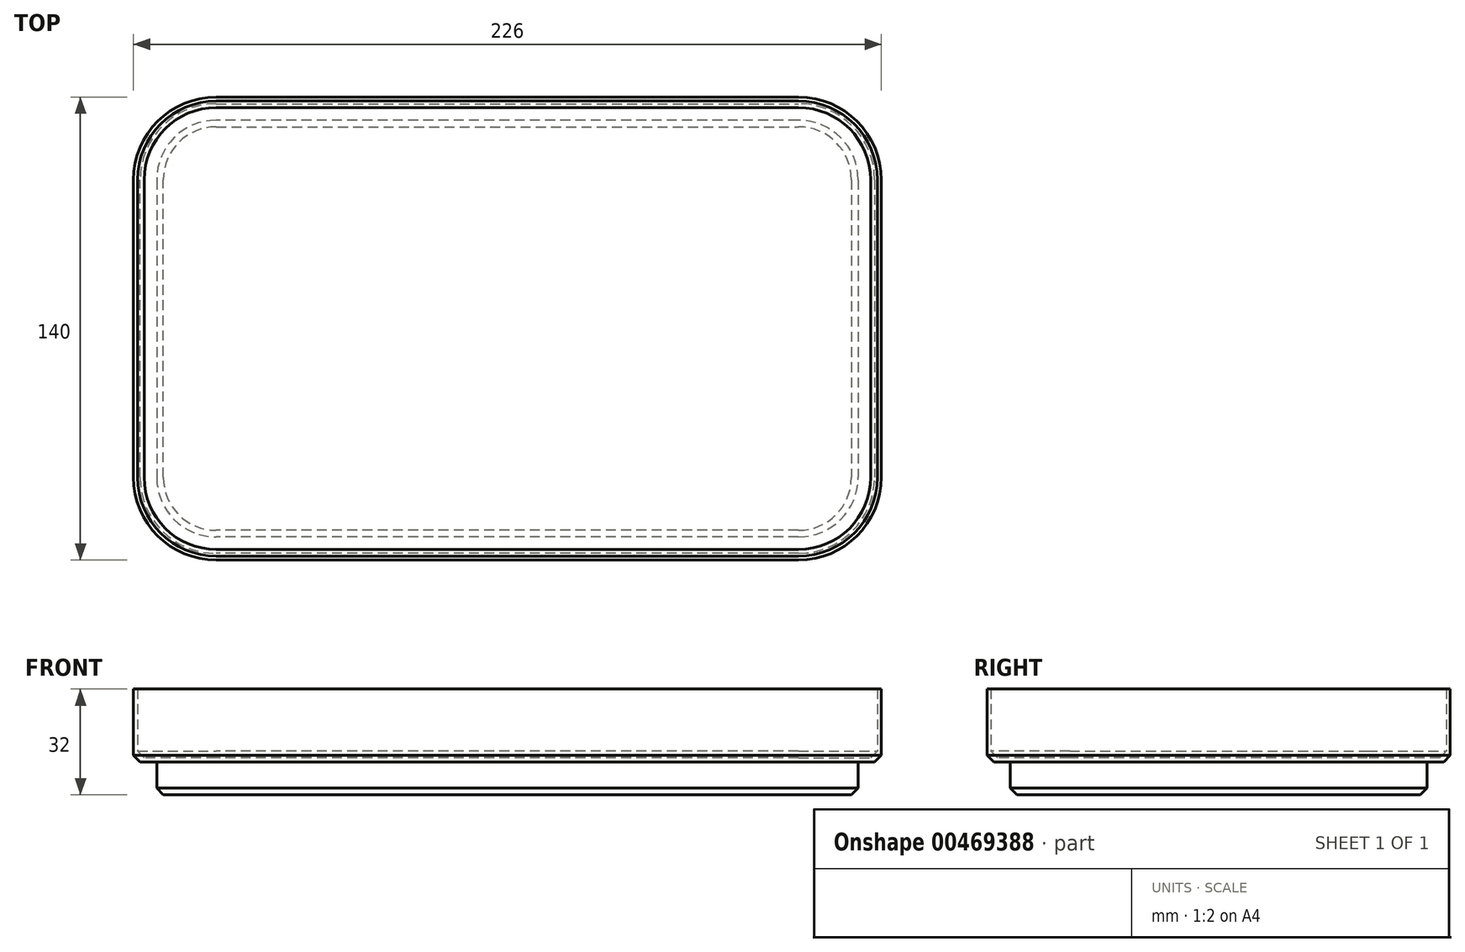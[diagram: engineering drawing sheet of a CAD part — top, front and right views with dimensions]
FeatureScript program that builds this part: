
annotation { "Feature Type Name" : "Feature", "Feature Type Description" : "" }
export const myFeature = defineFeature(function(context is Context, id is Id, definition is map)
    precondition{}
    {
        {
            var Q0;
            Q0=qCreatedBy(makeId("Top.planeOp"),FACE);
            var sketch = newSketch(context, id + "F0", { "sketchPlane" : qUnion([Q0])});
            skLineSegment(sketch, "E0.bottom", {"start": v(88, 70) * mm, "end": v(-88, 70) * mm});
            skLineSegment(sketch, "E0.top", {"start": v(88, -70) * mm, "end": v(-88, -70) * mm});
            skLineSegment(sketch, "E0.left", {"start": v(113, 45) * mm, "end": v(113, -45) * mm});
            skLineSegment(sketch, "E0.right", {"start": v(-113, 45) * mm, "end": v(-113, -45) * mm});
            skPoint(sketch, "E0.middle", {"position": v(0, 0) * mm});
            skPoint(sketch, "E1.visualSharp", {"position": v(-113, 70) * mm});
            skArc(sketch, "E1.filletArc", {"start": v(-88, 70) * mm, "mid": v(-105.68, 62.68) * mm, "end": v(-113, 45) * mm});
            skPoint(sketch, "E2.visualSharp", {"position": v(-113, -70) * mm});
            skArc(sketch, "E2.filletArc", {"start": v(-113, -45) * mm, "mid": v(-105.68, -62.68) * mm, "end": v(-88, -70) * mm});
            skPoint(sketch, "E3.visualSharp", {"position": v(113, -70) * mm});
            skArc(sketch, "E3.filletArc", {"start": v(88, -70) * mm, "mid": v(105.68, -62.68) * mm, "end": v(113, -45) * mm});
            skPoint(sketch, "E4.visualSharp", {"position": v(113, 70) * mm});
            skArc(sketch, "E4.filletArc", {"start": v(113, 45) * mm, "mid": v(105.68, 62.68) * mm, "end": v(88, 70) * mm});
            skArc(sketch, "E5.0", {"start": v(88, -63) * mm, "mid": v(100.73, -57.73) * mm, "end": v(106, -45) * mm});
            skLineSegment(sketch, "E5.1", {"start": v(106, 45) * mm, "end": v(106, -45) * mm});
            skLineSegment(sketch, "E5.2", {"start": v(88, -63) * mm, "end": v(-88, -63) * mm});
            skArc(sketch, "E5.3", {"start": v(106, 45) * mm, "mid": v(100.73, 57.73) * mm, "end": v(88, 63) * mm});
            skArc(sketch, "E5.4", {"start": v(-106, -45) * mm, "mid": v(-100.73, -57.73) * mm, "end": v(-88, -63) * mm});
            skLineSegment(sketch, "E5.5", {"start": v(-106, 45) * mm, "end": v(-106, -45) * mm});
            skArc(sketch, "E5.6", {"start": v(-88, 63) * mm, "mid": v(-100.73, 57.73) * mm, "end": v(-106, 45) * mm});
            skLineSegment(sketch, "E5.7", {"start": v(88, 63) * mm, "end": v(-88, 63) * mm});
            skLineSegment(sketch, "E6.0", {"start": v(88, -60.6) * mm, "end": v(-88, -60.6) * mm});
            skArc(sketch, "E6.1", {"start": v(-103.6, -45) * mm, "mid": v(-99.03, -56.03) * mm, "end": v(-88, -60.6) * mm});
            skArc(sketch, "E6.2", {"start": v(88, -60.6) * mm, "mid": v(99.03, -56.03) * mm, "end": v(103.6, -45) * mm});
            skLineSegment(sketch, "E6.3", {"start": v(-103.6, 45) * mm, "end": v(-103.6, -45) * mm});
            skLineSegment(sketch, "E6.4", {"start": v(103.6, 45) * mm, "end": v(103.6, -45) * mm});
            skArc(sketch, "E6.5", {"start": v(103.6, 45) * mm, "mid": v(99.03, 56.03) * mm, "end": v(88, 60.6) * mm});
            skLineSegment(sketch, "E6.6", {"start": v(88, 60.6) * mm, "end": v(-88, 60.6) * mm});
            skArc(sketch, "E6.7", {"start": v(-88, 60.6) * mm, "mid": v(-99.03, 56.03) * mm, "end": v(-103.6, 45) * mm});
            skSolve(sketch);
        }
        {
            var Q0;
            Q0 = qSketchRegion(id + "F0", true);
            var Q1;
            Q1=makeQuery(id+"F0.imprint","IMPRINT",FACE,{"disambiguationData":[TD([[makeQuery(id+"F0.imprint","IMPRINT",EDGE,{"derivedFrom":sQuery(id+"F0.wireOp",EDGE,"E5.0")}),1.0]])]});
            var Q2;
            Q2=makeQuery(id+"F0.imprint","IMPRINT",FACE,{"disambiguationData":[TD([[makeQuery(id+"F0.imprint","IMPRINT",EDGE,{"derivedFrom":sQuery(id+"F0.wireOp",EDGE,"E6.0")}),-1.0]])]});
            extrude(context, id + "F1", {"entities" : qUnion([Q0, Q1, Q2]), "depth" : 22 * mm, "offsetDistance" : 25 * mm});
        }
        {
            var Q0;
            Q0=makeQuery(id+"F1.opExtrude","CAP_FACE",FACE,{"disambiguationData":[OSD([sQuery(id+"F0.wireOp",EDGE,"E0.bottom"),sQuery(id+"F0.wireOp",EDGE,"E0.top"),sQuery(id+"F0.wireOp",EDGE,"E0.left"),sQuery(id+"F0.wireOp",EDGE,"E0.right"),sQuery(id+"F0.wireOp",EDGE,"E1.filletArc"),sQuery(id+"F0.wireOp",EDGE,"E2.filletArc"),sQuery(id+"F0.wireOp",EDGE,"E3.filletArc"),sQuery(id+"F0.wireOp",EDGE,"E4.filletArc")])],"isStart":false});
            shell(context, id + "F2", {"entities" : qUnion([Q0]), "thickness" : 1.2 * mm});
        }
        {
            var Q0;
            Q0=makeQuery(id+"F0.imprint","IMPRINT",FACE,{"disambiguationData":[TD([[makeQuery(id+"F0.imprint","IMPRINT",EDGE,{"derivedFrom":sQuery(id+"F0.wireOp",EDGE,"E5.0")}),1.0]])]});
            var Q1;
            Q1=makeQuery(id+"F0.imprint","IMPRINT",FACE,{"disambiguationData":[TD([[makeQuery(id+"F0.imprint","IMPRINT",EDGE,{"derivedFrom":sQuery(id+"F0.wireOp",EDGE,"E6.0")}),-1.0]])]});
            extrude(context, id + "F3", {"entities" : qUnion([Q0, Q1]), "operationType" : NewBodyOperationType.ADD, "oppositeDirection" : true, "depth" : 10 * mm, "offsetDistance" : 25 * mm});
        }
        {
            var Q0;
            Q0=makeQuery(id+"F3.opExtrude","CAP_FACE",FACE,{"disambiguationData":[OSD([sQuery(id+"F0.wireOp",EDGE,"E5.0"),sQuery(id+"F0.wireOp",EDGE,"E5.1"),sQuery(id+"F0.wireOp",EDGE,"E5.2"),sQuery(id+"F0.wireOp",EDGE,"E5.3"),sQuery(id+"F0.wireOp",EDGE,"E5.4"),sQuery(id+"F0.wireOp",EDGE,"E5.5"),sQuery(id+"F0.wireOp",EDGE,"E5.6"),sQuery(id+"F0.wireOp",EDGE,"E5.7")])],"isStart":false});
            var Q1;
            Q1=makeQuery(id+"F1.opExtrude","CAP_EDGE",EDGE,{"disambiguationData":[OSD([sQuery(id+"F0.wireOp",EDGE,"E0.right")])],"isStart":true});
            var Q2;
            Q2=makeQuery(id+"F1.opExtrude","CAP_EDGE",EDGE,{"disambiguationData":[OSD([sQuery(id+"F0.wireOp",EDGE,"E2.filletArc")])],"isStart":true});
            var Q3;
            Q3=makeQuery(id+"F1.opExtrude","CAP_EDGE",EDGE,{"disambiguationData":[OSD([sQuery(id+"F0.wireOp",EDGE,"E0.top")])],"isStart":true});
            var Q4;
            Q4=makeQuery(id+"F1.opExtrude","CAP_EDGE",EDGE,{"disambiguationData":[OSD([sQuery(id+"F0.wireOp",EDGE,"E1.filletArc")])],"isStart":true});
            var Q5;
            Q5=makeQuery(id+"F1.opExtrude","CAP_EDGE",EDGE,{"disambiguationData":[OSD([sQuery(id+"F0.wireOp",EDGE,"E0.bottom")])],"isStart":true});
            var Q6;
            Q6=makeQuery(id+"F1.opExtrude","CAP_EDGE",EDGE,{"disambiguationData":[OSD([sQuery(id+"F0.wireOp",EDGE,"E4.filletArc")])],"isStart":true});
            var Q7;
            Q7=makeQuery(id+"F1.opExtrude","CAP_EDGE",EDGE,{"disambiguationData":[OSD([sQuery(id+"F0.wireOp",EDGE,"E3.filletArc")])],"isStart":true});
            var Q8;
            Q8=makeQuery(id+"F1.opExtrude","CAP_EDGE",EDGE,{"disambiguationData":[OSD([sQuery(id+"F0.wireOp",EDGE,"E0.left")])],"isStart":true});
            chamfer(context, id + "F4", {"entities" : qUnion([Q0, Q1, Q2, Q3, Q4, Q5, Q6, Q7, Q8]), "width" : 2 * mm, "tangentPropagation" : true});
        }
        {
            var Q0;
            Q0=makeQuery(id+"F2.opShell","OFFSET_FACE",FACE,{"disambiguationData":[OSD([sQuery(id+"F0.wireOp",EDGE,"E0.bottom"),sQuery(id+"F0.wireOp",EDGE,"E0.top"),sQuery(id+"F0.wireOp",EDGE,"E0.left"),sQuery(id+"F0.wireOp",EDGE,"E0.right"),sQuery(id+"F0.wireOp",EDGE,"E1.filletArc"),sQuery(id+"F0.wireOp",EDGE,"E2.filletArc"),sQuery(id+"F0.wireOp",EDGE,"E3.filletArc"),sQuery(id+"F0.wireOp",EDGE,"E4.filletArc")])]});
            chamfer(context, id + "F5", {"entities" : qUnion([Q0]), "width" : 2 * mm, "tangentPropagation" : true});
        }
    });
